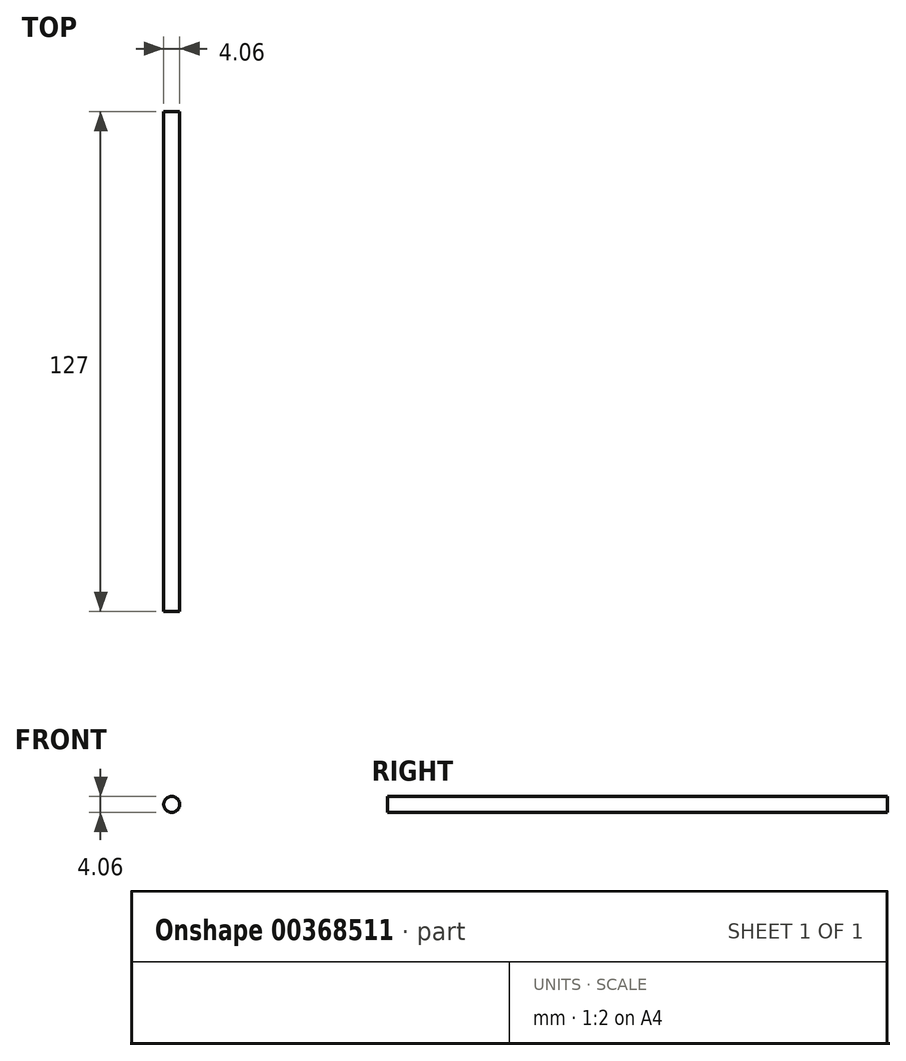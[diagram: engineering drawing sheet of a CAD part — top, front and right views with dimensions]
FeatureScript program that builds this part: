
annotation { "Feature Type Name" : "Feature", "Feature Type Description" : "" }
export const myFeature = defineFeature(function(context is Context, id is Id, definition is map)
    precondition{}
    {
        {
            var Q0;
            Q0=qCreatedBy(makeId("Front.planeOp"),FACE);
            var sketch = newSketch(context, id + "F0", { "sketchPlane" : qUnion([Q0])});
            skCircle(sketch, "E0", {"center": v(0, 0) * mm, "radius": 2.03 * mm});
            skSolve(sketch);
        }
        {
            var Q0;
            Q0=makeQuery(id+"F0.imprint","IMPRINT",FACE,{"disambiguationData":[TD([[makeQuery(id+"F0.imprint","IMPRINT",EDGE,{"derivedFrom":sQuery(id+"F0.wireOp",EDGE,"E0")}),1.0]])]});
            extrude(context, id + "F1", {"entities" : qUnion([Q0]), "depth" : 127 * mm, "symmetric" : true});
        }
    });
